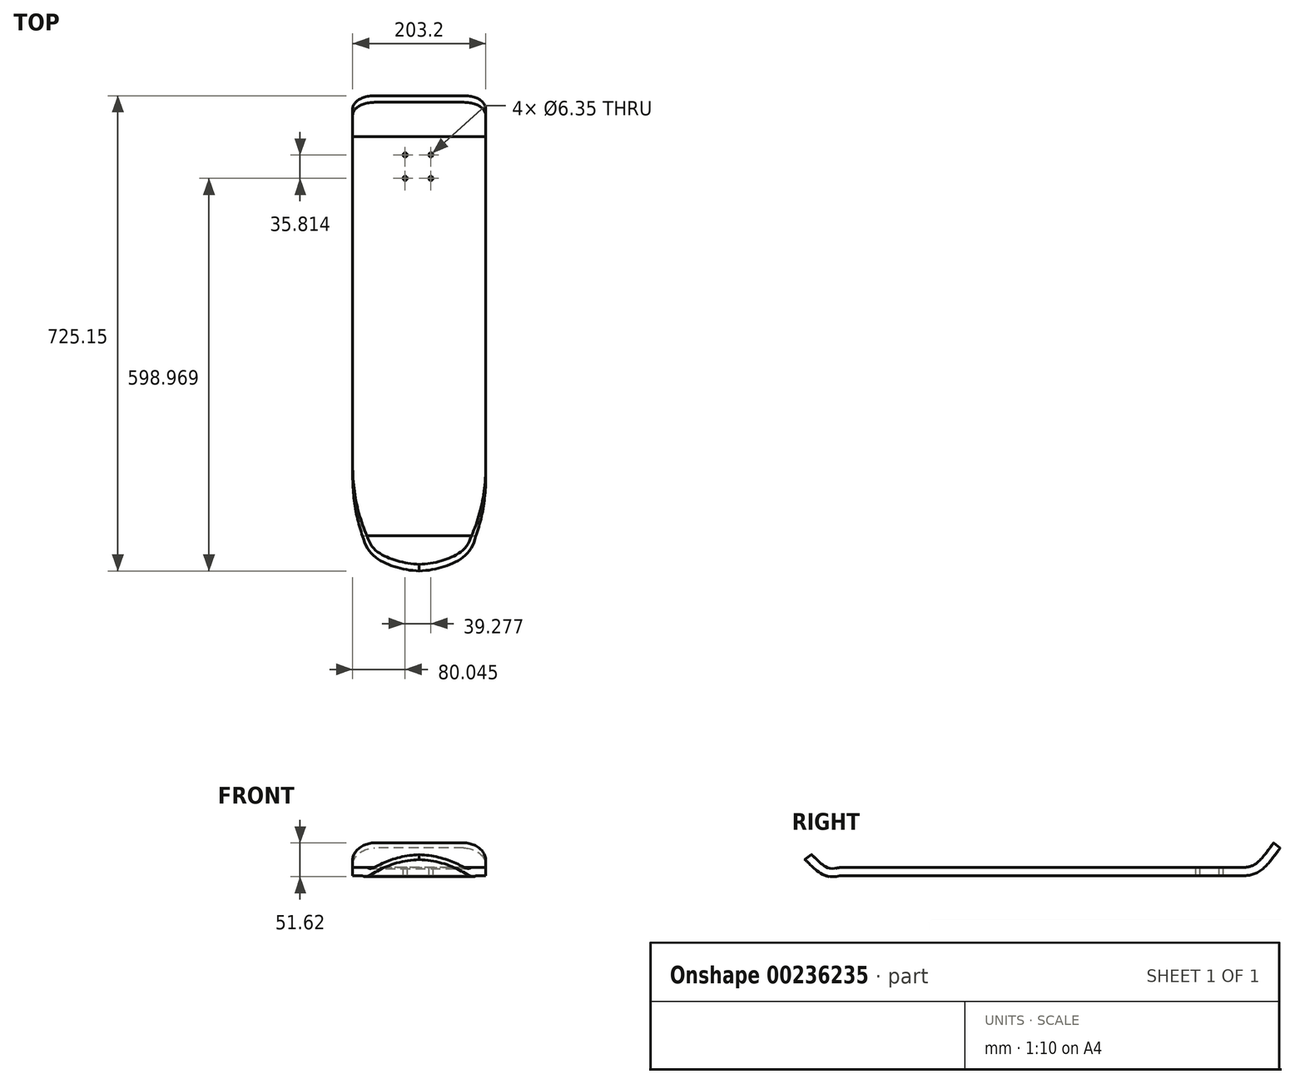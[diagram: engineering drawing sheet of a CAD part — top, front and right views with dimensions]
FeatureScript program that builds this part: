
annotation { "Feature Type Name" : "Feature", "Feature Type Description" : "" }
export const myFeature = defineFeature(function(context is Context, id is Id, definition is map)
    precondition{}
    {
        {
            var Q0;
            Q0=qCreatedBy(makeId("Top.planeOp"),FACE);
            var sketch = newSketch(context, id + "F0", { "sketchPlane" : qUnion([Q0])});
            skLineSegment(sketch, "E0.bottom", {"start": v(101.6, -304.8) * mm, "end": v(-101.6, -304.8) * mm});
            skLineSegment(sketch, "E0.top", {"start": v(101.6, 304.8) * mm, "end": v(-101.6, 304.8) * mm});
            skLineSegment(sketch, "E0.left", {"start": v(101.6, -304.8) * mm, "end": v(101.6, 304.8) * mm});
            skLineSegment(sketch, "E0.right", {"start": v(-101.6, -304.8) * mm, "end": v(-101.6, 304.8) * mm});
            skPoint(sketch, "E0.middle", {"position": v(0, 0) * mm});
            skCircle(sketch, "E1", {"center": v(-21.56, 241.44) * mm, "radius": 3.18 * mm});
            skCircle(sketch, "E2", {"center": v(-21.56, 277.25) * mm, "radius": 3.18 * mm});
            skCircle(sketch, "E3", {"center": v(17.72, 241.44) * mm, "radius": 3.18 * mm});
            skCircle(sketch, "E4", {"center": v(17.72, 277.25) * mm, "radius": 3.18 * mm});
            skSolve(sketch);
        }
        {
            var Q0;
            Q0 = qSketchRegion(id + "F0", true);
            extrude(context, id + "F1", {"entities" : qUnion([Q0]), "endBound" : BoundingType.SYMMETRIC, "depth" : 12.7 * mm});
        }
        {
            var Q0;
            Q0=qCreatedBy(makeId("Right.planeOp"),FACE);
            var sketch = newSketch(context, id + "F2", { "sketchPlane" : qUnion([Q0])});
            skFitSpline(sketch, "E5", {"points": [v(307.06, 0) * mm, v(331.36, 5.26) * mm, v(363.96, 42) * mm], "startDerivative": vector(59, 2.2) * mm, "endDerivative": vector(55, 77.56) * mm});
            skFitSpline(sketch, "E6", {"points": [v(-304.1, 0) * mm, v(-324.46, 0) * mm, v(-343.64, 13.71) * mm, v(-352.63, 22.37) * mm], "startDerivative": vector(-63.94, -9.83) * mm, "endDerivative": vector(-42.92, 41.82) * mm});
            skSolve(sketch);
        }
        {
            var Q0;
            Q0=makeQuery(id+"F1.opExtrude","SWEPT_FACE",FACE,{"disambiguationData":[OSD([sQuery(id+"F0.wireOp",EDGE,"E0.top")])]});
            var Q1;
            Q1=sQuery(id+"F2.wireOp",EDGE,"E5");
            sweep(context, id + "F3", {"operationType" : NewBodyOperationType.ADD, "profiles" : qUnion([Q0]), "path" : qUnion([Q1])});
        }
        {
            var Q0;
            Q0=makeQuery(id+"F1.opExtrude","SWEPT_FACE",FACE,{"disambiguationData":[OSD([sQuery(id+"F0.wireOp",EDGE,"E0.bottom")])]});
            var Q1;
            Q1=sQuery(id+"F2.wireOp",EDGE,"E6");
            sweep(context, id + "F4", {"operationType" : NewBodyOperationType.ADD, "profiles" : qUnion([Q0]), "path" : qUnion([Q1])});
        }
        {
            var Q0;
            Q0=makeQuery(id+"F4.opSweep","CAP_EDGE",EDGE,{"disambiguationData":[OSD([sQuery(id+"F0.wireOp",EDGE,"E0.bottom"),sQuery(id+"F0.wireOp",EDGE,"E0.left"),sQuery(id+"F2.wireOp",VERTEX,"E6.end")])],"isStart":false});
            var Q1;
            Q1=makeQuery(id+"F4.opSweep","CAP_EDGE",EDGE,{"disambiguationData":[OSD([sQuery(id+"F0.wireOp",EDGE,"E0.bottom"),sQuery(id+"F0.wireOp",EDGE,"E0.right"),sQuery(id+"F2.wireOp",VERTEX,"E6.end")])],"isStart":false});
            fillet(context, id + "F5", {"entities" : qUnion([Q0, Q1]), "radius" : 106.7 * mm, "tangentPropagation" : true, "allowEdgeOverflow" : false});
        }
        {
            var Q0;
            Q0=makeQuery(id+"F3.opSweep","CAP_EDGE",EDGE,{"disambiguationData":[OSD([sQuery(id+"F0.wireOp",EDGE,"E0.top"),sQuery(id+"F0.wireOp",EDGE,"E0.left"),sQuery(id+"F2.wireOp",VERTEX,"E5.end")])],"isStart":false});
            var Q1;
            Q1=makeQuery(id+"F3.opSweep","CAP_EDGE",EDGE,{"disambiguationData":[OSD([sQuery(id+"F0.wireOp",EDGE,"E0.top"),sQuery(id+"F0.wireOp",EDGE,"E0.right"),sQuery(id+"F2.wireOp",VERTEX,"E5.end")])],"isStart":false});
            fillet(context, id + "F6", {"entities" : qUnion([Q0, Q1]), "radius" : 33.73 * mm, "tangentPropagation" : true, "allowEdgeOverflow" : false});
        }
    });
